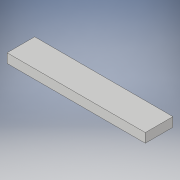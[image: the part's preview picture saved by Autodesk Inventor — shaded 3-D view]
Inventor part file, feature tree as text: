
AUTODESK INVENTOR PART (.ipt)
format: ipt  version: 2019 (Build 230136000, 136)  size: 90,112 bytes
history: native  units: mm
features: extrude x1, sketch x1
ambient origin geometry x8: Origin, YZ Plane, XZ Plane, XY Plane, X Axis, Y Axis, Z Axis, Center Point
bodies: Solid1 (feature_tree)
feature tree (2):
  extrude  "Extrusion1"  Depth=30.0mm
  sketch  "Sketch1"  dims[d0=150.0mm d1=30.0mm d2=10.0mm d3=0.0mm]
